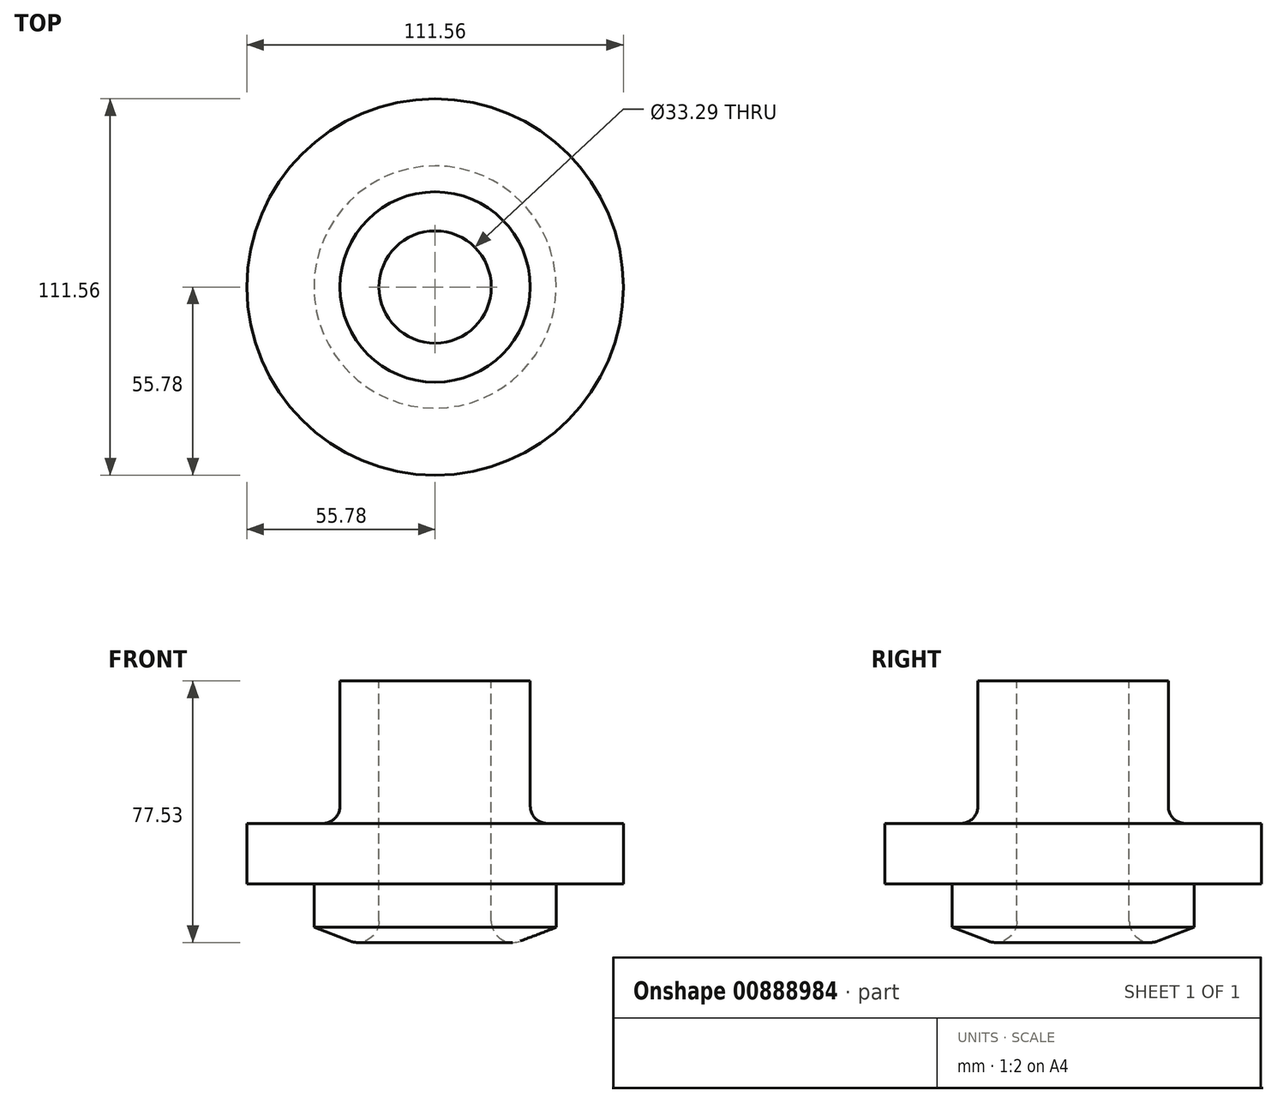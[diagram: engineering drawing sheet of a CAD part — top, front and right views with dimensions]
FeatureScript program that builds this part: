
annotation { "Feature Type Name" : "Feature", "Feature Type Description" : "" }
export const myFeature = defineFeature(function(context is Context, id is Id, definition is map)
    precondition{}
    {
        {
            var Q0;
            Q0=qCreatedBy(makeId("Top.planeOp"),FACE);
            var sketch = newSketch(context, id + "F0", { "sketchPlane" : qUnion([Q0])});
            skLineSegment(sketch, "E0", {"start": v(-91.36, 33.36) * mm, "end": v(-91.36, -25.4) * mm});
            skLineSegment(sketch, "E1", {"start": v(-91.36, -25.4) * mm, "end": v(-15.04, -78.54) * mm});
            skLineSegment(sketch, "E2", {"start": v(-15.04, -78.54) * mm, "end": v(38.1, -25.4) * mm});
            skLineSegment(sketch, "E3", {"start": v(38.1, -25.4) * mm, "end": v(38.1, 50.8) * mm});
            skLineSegment(sketch, "E4", {"start": v(38.1, 50.8) * mm, "end": v(-39.77, 50.8) * mm});
            skLineSegment(sketch, "E5", {"start": v(-39.77, 50.8) * mm, "end": v(-91.36, 33.36) * mm});
            skLineSegment(sketch, "E6", {"start": v(0, 0) * mm, "end": v(-51.11, 0) * mm, "construction": true});
            skCircle(sketch, "E7", {"center": v(0, 0) * mm, "radius": 19.05 * mm});
            skSolve(sketch);
        }
        {
            var Q0;
            Q0=qCreatedBy(makeId("Front.planeOp"),FACE);
            var sketch = newSketch(context, id + "F1", { "sketchPlane" : qUnion([Q0])});
            skLineSegment(sketch, "E8", {"start": v(-28.21, 50.73) * mm, "end": v(-28.21, 8.5) * mm});
            skLineSegment(sketch, "E9", {"start": v(-28.21, 8.5) * mm, "end": v(-55.78, 8.5) * mm});
            skLineSegment(sketch, "E10", {"start": v(-55.78, 8.5) * mm, "end": v(-55.78, -9.49) * mm});
            skLineSegment(sketch, "E11", {"start": v(-55.78, -9.49) * mm, "end": v(-35.9, -9.49) * mm});
            skLineSegment(sketch, "E12", {"start": v(-35.9, -9.49) * mm, "end": v(-35.9, -22.34) * mm});
            skLineSegment(sketch, "E13", {"start": v(-16.64, -20.45) * mm, "end": v(-16.64, 50.73) * mm});
            skLineSegment(sketch, "E14", {"start": v(-16.64, 50.73) * mm, "end": v(-28.21, 50.73) * mm});
            skLineSegment(sketch, "E15", {"start": v(-35.9, -22.34) * mm, "end": v(-25.25, -26.39) * mm});
            skLineSegment(sketch, "E16", {"start": v(0, 0) * mm, "end": v(0, -51.5) * mm, "construction": true});
            skPoint(sketch, "E17.visualSharp", {"position": v(-16.64, -29.66) * mm});
            skArc(sketch, "E17.filletArc", {"start": v(-25.25, -26.39) * mm, "mid": v(-19.39, -25.68) * mm, "end": v(-16.64, -20.45) * mm});
            skSolve(sketch);
        }
        {
            var Q0;
            Q0=makeQuery(id+"F1.imprint","IMPRINT",FACE,{"disambiguationData":[TD([[makeQuery(id+"F1.imprint","IMPRINT",EDGE,{"derivedFrom":sQuery(id+"F1.wireOp",EDGE,"E8")}),1.0]])]});
            var Q1;
            Q1=sQuery(id+"F1.wireOp",EDGE,"E16");
            var Q2;
            Q2=sQuery(id+"F1.wireOp",EDGE,"E16");
            revolve(context, id + "F2", {"surfaceOperationType" : NewSurfaceOperationType.NEW, "entities" : qUnion([Q0]), "surfaceEntities" : qUnion([Q1]), "axis" : qUnion([Q2]), "revolveType" : RevolveType.FULL});
        }
        {
            var Q0;
            Q0=makeQuery(id+"F2.opRevolve","SWEPT_EDGE",EDGE,{"disambiguationData":[OSD([sQuery(id+"F1.wireOp",EDGE,"E8"),sQuery(id+"F1.wireOp",EDGE,"E9")])]});
            fillet(context, id + "F3", {"entities" : qUnion([Q0]), "radius" : 5.08 * mm, "tangentPropagation" : true, "allowEdgeOverflow" : false});
        }
    });
